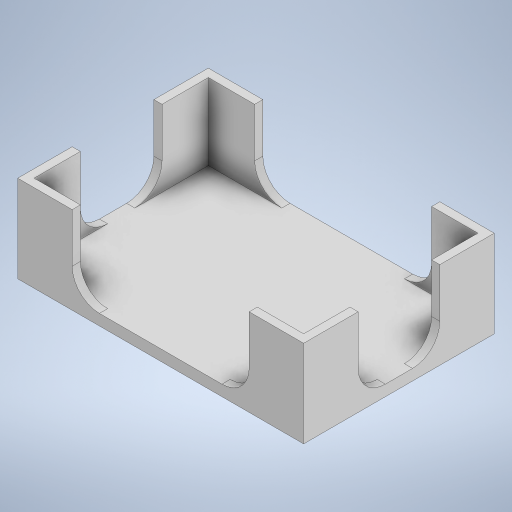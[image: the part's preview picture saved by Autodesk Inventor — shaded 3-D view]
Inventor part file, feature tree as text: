
AUTODESK INVENTOR PART (.ipt)
format: ipt  version: 2024.2 (Build 282272000, 272)  size: 291,840 bytes
history: native  units: mm
features: extrude x2, sketch x2, fillet x1
ambient origin geometry x8: Origin, YZ Plane, XZ Plane, XY Plane, X Axis, Y Axis, Z Axis, Center Point
bodies: Solid1 (feature_tree)
feature tree (5):
  extrude  "Extrusion1"  Depth=70.0mm
  extrude  "Extrusion3"  Depth=20.0mm
  fillet  "Fillet2"  Radius=3.0mm
  sketch  "Sketch1"  dims[d0=105.0mm d1=70.0mm]
  sketch  "Sketch3"  dims[d2=4.0mm d3=0.0mm d15=20.0mm d16=3.0mm d17=20.0mm d18=3.0mm d19=52.5mm d20=35.0mm d21=28.0mm d22=0.0mm d23=10.0mm]
